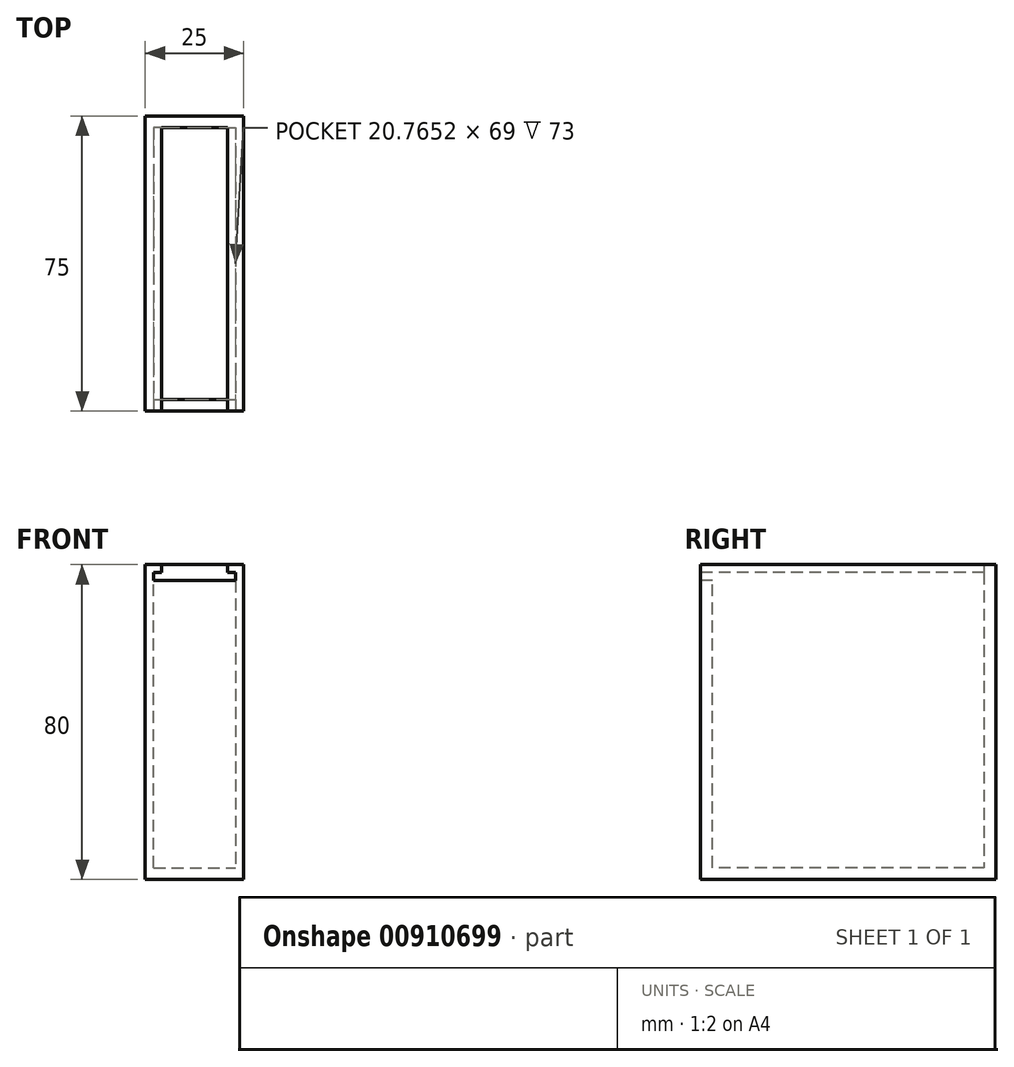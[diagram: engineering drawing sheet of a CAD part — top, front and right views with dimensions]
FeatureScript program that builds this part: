
annotation { "Feature Type Name" : "Feature", "Feature Type Description" : "" }
export const myFeature = defineFeature(function(context is Context, id is Id, definition is map)
    precondition{}
    {
        {
            var Q0;
            Q0=qCreatedBy(makeId("Front.planeOp"),FACE);
            var sketch = newSketch(context, id + "F0", { "sketchPlane" : qUnion([Q0])});
            skLineSegment(sketch, "E0.bottom", {"start": v(-12.5, 40) * mm, "end": v(12.5, 40) * mm});
            skLineSegment(sketch, "E0.top", {"start": v(-12.5, -40) * mm, "end": v(12.5, -40) * mm});
            skLineSegment(sketch, "E0.left", {"start": v(-12.5, 40) * mm, "end": v(-12.5, -40) * mm});
            skLineSegment(sketch, "E0.right", {"start": v(12.5, 40) * mm, "end": v(12.5, -40) * mm});
            skPoint(sketch, "E0.middle", {"position": v(0, 0) * mm});
            skSolve(sketch);
        }
        {
            var Q0;
            Q0=makeQuery(id+"F0.imprint","IMPRINT",FACE,{"disambiguationData":[TD([[makeQuery(id+"F0.imprint","IMPRINT",EDGE,{"derivedFrom":sQuery(id+"F0.wireOp",EDGE,"E0.bottom")}),-1.0]])]});
            extrude(context, id + "F1", {"entities" : qUnion([Q0]), "endBound" : BoundingType.SYMMETRIC, "depth" : 75 * mm, "offsetDistance" : 25 * mm});
        }
        {
            var Q0;
            Q0=makeQuery(id+"F1.opExtrude","CAP_FACE",FACE,{"disambiguationData":[OSD([sQuery(id+"F0.wireOp",EDGE,"E0.bottom"),sQuery(id+"F0.wireOp",EDGE,"E0.top"),sQuery(id+"F0.wireOp",EDGE,"E0.left"),sQuery(id+"F0.wireOp",EDGE,"E0.right")])],"isStart":false});
            var sketch = newSketch(context, id + "F2", { "sketchPlane" : qUnion([Q0])});
            skLineSegment(sketch, "E1", {"start": v(8.36, 40) * mm, "end": v(8.36, 38) * mm});
            skLineSegment(sketch, "E2", {"start": v(8.36, 38) * mm, "end": v(10.38, 38) * mm});
            skLineSegment(sketch, "E3", {"start": v(10.38, 38) * mm, "end": v(10.38, 36) * mm});
            skLineSegment(sketch, "E4", {"start": v(10.38, 36) * mm, "end": v(0, 36) * mm});
            skLineSegment(sketch, "E5.MirrorCS", {"start": v(0, 40) * mm, "end": v(-8.36, 40) * mm});
            skLineSegment(sketch, "E6.MirrorCS", {"start": v(-8.36, 40) * mm, "end": v(-8.36, 38) * mm});
            skLineSegment(sketch, "E7.MirrorCS", {"start": v(-10.38, 38) * mm, "end": v(-10.38, 36) * mm});
            skLineSegment(sketch, "E8.MirrorCS", {"start": v(-10.38, 36) * mm, "end": v(0, 36) * mm});
            skLineSegment(sketch, "E9.MirrorCS", {"start": v(-8.36, 38) * mm, "end": v(-10.38, 38) * mm});
            skLineSegment(sketch, "E10", {"start": v(0, 40) * mm, "end": v(8.36, 40) * mm});
            skSolve(sketch);
        }
        {
            var Q0;
            Q0=makeQuery(id+"F2.imprint","IMPRINT",FACE,{"disambiguationData":[TD([[makeQuery(id+"F2.imprint","IMPRINT",EDGE,{"derivedFrom":sQuery(id+"F2.wireOp",EDGE,"E1")}),-1.0]])]});
            extrude(context, id + "F3", {"entities" : qUnion([Q0]), "operationType" : NewBodyOperationType.REMOVE, "oppositeDirection" : true, "depth" : 72 * mm, "offsetDistance" : 25 * mm});
        }
        {
            var Q0;
            Q0=makeQuery(id+"F3.boolean.opBoolean","COPY",FACE,{"derivedFrom":makeQuery(id+"F3.opExtrude","SWEPT_FACE",FACE,{"disambiguationData":[OSD([sQuery(id+"F2.wireOp",EDGE,"E8.MirrorCS"),sQuery(id+"F2.wireOp",EDGE,"E4")])]})});
            var sketch = newSketch(context, id + "F4", { "sketchPlane" : qUnion([Q0])});
            skLineSegment(sketch, "E11.bottom", {"start": v(-10.38, 34.5) * mm, "end": v(10.38, 34.5) * mm});
            skLineSegment(sketch, "E11.top", {"start": v(-10.38, -34.5) * mm, "end": v(10.38, -34.5) * mm});
            skLineSegment(sketch, "E11.left", {"start": v(-10.38, 34.5) * mm, "end": v(-10.38, -34.5) * mm});
            skLineSegment(sketch, "E11.right", {"start": v(10.38, 34.5) * mm, "end": v(10.38, -34.5) * mm});
            skPoint(sketch, "E11.middle", {"position": v(0, 0) * mm});
            skSolve(sketch);
        }
        {
            var Q0;
            Q0=makeQuery(id+"F4.imprint","IMPRINT",FACE,{"disambiguationData":[TD([[makeQuery(id+"F4.imprint","IMPRINT",EDGE,{"derivedFrom":sQuery(id+"F4.wireOp",EDGE,"E11.bottom")}),-1.0]])]});
            extrude(context, id + "F5", {"entities" : qUnion([Q0]), "operationType" : NewBodyOperationType.REMOVE, "oppositeDirection" : true, "depth" : 73 * mm, "offsetDistance" : 25 * mm});
        }
    });
